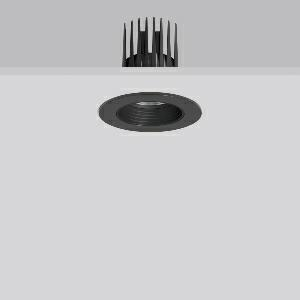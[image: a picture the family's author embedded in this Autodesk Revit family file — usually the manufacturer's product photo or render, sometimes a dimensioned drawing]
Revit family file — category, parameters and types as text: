
# Revit family: heledon_mini_e_901755_003_2_939f
name_source: partatom
category: Lighting Fixtures
units: mm (PartAtom-declared; Revit-internal decimal feet)

## family parameters
Cut with Voids When Loaded = No
Host = Face
Light Source = No
Part Type = Normal
Room Calculation Point = No
Round Connector Dimension = Use Diameter
Shared = No

## types (1)
- HELEDON mini E (1 x LED Modul 927, 2600 lm, 2700)
    Apparent Load = 29 VA
    Approval mark = CE
    CIE Flux Codes = 95 100 100 100 100
    Color Rendering = 92
    Color Temperature = 2700
    Default Elevation = 1800 mm
    Description = Series: HELEDON mini
Round recessed downlight. Housing: die-cast aluminium, powder-coated. Black plastic ring and recessed LED to prevent glare from the side. Optical assembly with lens made of plastic (polycarbonate) for the best homogeneous light distribution - can be changed without tools. Best colour rendering index Ra>90. Suitable for Recessed ceiling mounting. Installation without tools thanks to spring fastening system. Including separate LED converter with connecting cable 600 mm.High quality converter without flickering and stroboscopic effect. Through-wiring box (5 pole) available as accessory. The following accessories can be mounted without use of tools: interchangeable lenses, decorative glasses, honeycomb louvre, clear and frosted diffusers, white interchangeable plastic ring. 
Colour: deep black, matt (RAL 9005)
Diameter: 124 mm
Height: 3 mm
Cut-out diameter: 114 mm
Recess height: 170 mm
Luminaire: recess height: 120 mm
Lamp: LED
Socket: without socket
Colour temperature: 2700K
Colour rendering index (CRI): 92
System power: 29 W
Rated luminous flux: 2600 lm
Luminous efficiency: 90 lm/W
Control gear: Regulated power supply
Protection class: II
Type of protection: IP 20
    Height = 0 mm  [stored 0 ft]
    Lamp = 1 x LED Modul 927
    Lamp Light Flux = 2600 lm
    Lamp count = 1
    Length = 124 mm  [stored 0.406824 ft]
    Lifetime = 50000 h
    Luminous efficacy = 90 lm/W
    Manufacturer = RZB
    ModVariant = No
    Model = 901755.003.2
    Mounting Place = Ceiling
    Mounting Type = Recessed
    Number of Poles = 1
    OnlyDefault = Yes
    Power Factor = 1
    Product Name = HELEDON mini E
    Product group = Recessed downlights
    ProductGroupID = 402
    Protection Class = Protection class II
    Protection Degree = IP 20
    RLX_Detail_Level = 1
    RLX_Emergency_Light_Flux = 0 lm
    RLX_Emergency_Type = 0
    RLX_Emergency_Type_DB = No
    RlxData = <blob elided: 131273 chars, md5=ec9bdda3>
    Socket = socket
    Standby Power = 0 W
    System Light Flux = 2600 lm
    System Power = 29 W
    Type Comments = Product without accessories
    Type Image = 901656.003.jpg
    URL = http://relux.com
    VarID = ---
    Voltage = 230 V
    Voltage Range = 220-240 V
    Weight = 0.00 kg
    Width = 0 mm  [stored 0 ft]

note: [stored X ft] marks values corroborated as IEEE doubles in the binary element streams (Revit-internal decimal feet)

## geometry (parser evidence)
native form markers: Blend x4, Sweep x11
no freeform markers — native parametric forms only
